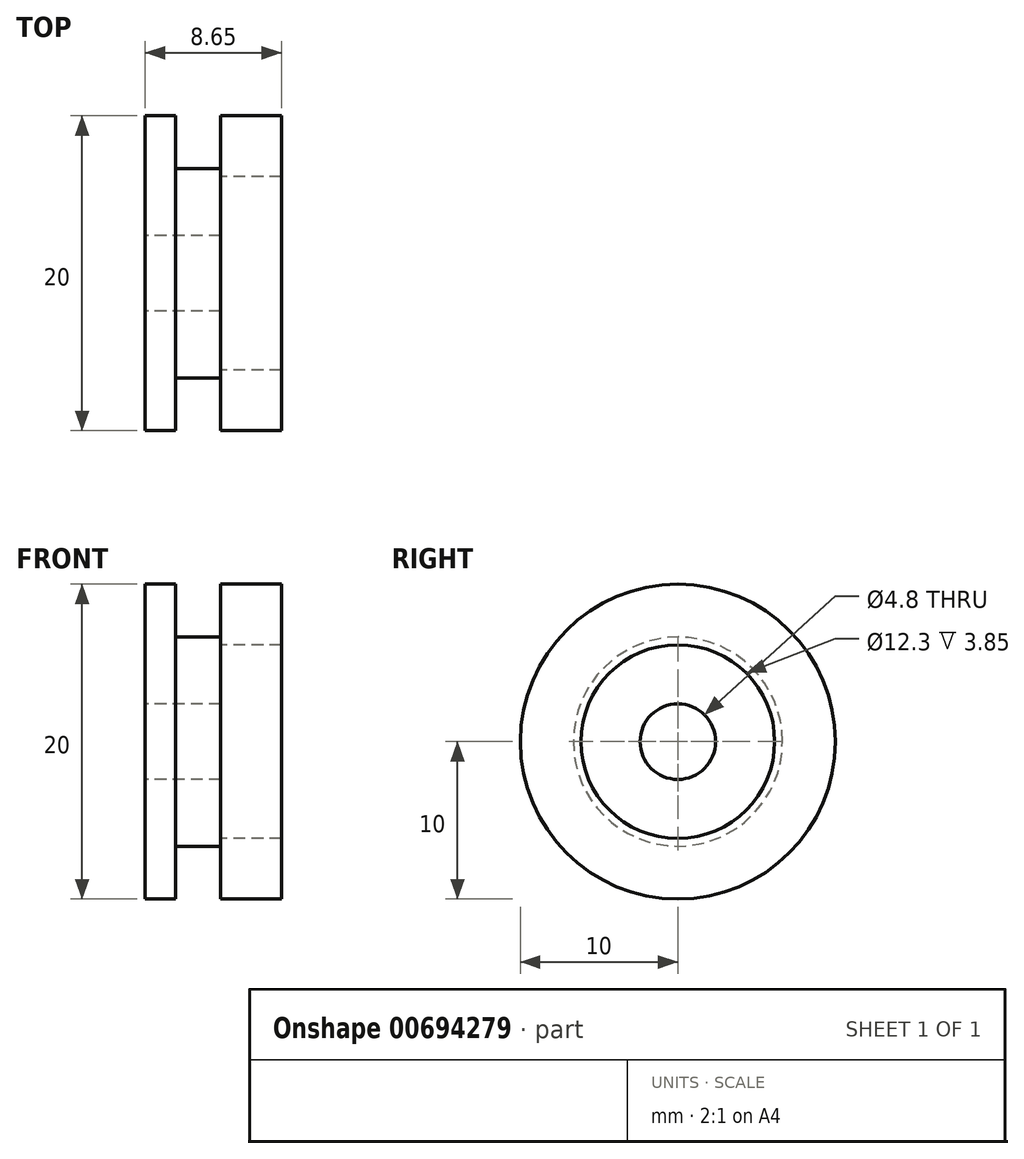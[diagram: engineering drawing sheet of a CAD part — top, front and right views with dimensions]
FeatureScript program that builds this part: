
annotation { "Feature Type Name" : "Feature", "Feature Type Description" : "" }
export const myFeature = defineFeature(function(context is Context, id is Id, definition is map)
    precondition{}
    {
        {
            var Q0;
            Q0=qCreatedBy(makeId("Front.planeOp"),FACE);
            var sketch = newSketch(context, id + "F0", { "sketchPlane" : qUnion([Q0])});
            skLineSegment(sketch, "E0", {"start": v(-5, 0) * mm, "end": v(-5, 10) * mm});
            skLineSegment(sketch, "E1", {"start": v(-5, 10) * mm, "end": v(-3.08, 10) * mm});
            skLineSegment(sketch, "E2", {"start": v(-3.08, 10) * mm, "end": v(-3.08, 6.64) * mm});
            skLineSegment(sketch, "E3", {"start": v(-3.08, 6.64) * mm, "end": v(-0.2, 6.64) * mm});
            skLineSegment(sketch, "E4", {"start": v(-0.2, 6.64) * mm, "end": v(-0.2, 10) * mm});
            skLineSegment(sketch, "E5", {"start": v(-0.2, 10) * mm, "end": v(3.65, 10) * mm});
            skPoint(sketch, "E6.end.orphan", {"position": v(-5, 2.4) * mm});
            skLineSegment(sketch, "E7", {"start": v(3.65, 10) * mm, "end": v(3.65, 6.15) * mm});
            skLineSegment(sketch, "E8", {"start": v(3.65, 6.15) * mm, "end": v(-0.2, 6.15) * mm});
            skLineSegment(sketch, "E9", {"start": v(-0.2, 6.15) * mm, "end": v(-0.2, 2.4) * mm});
            skLineSegment(sketch, "E10", {"start": v(-0.2, 2.4) * mm, "end": v(-5, 2.4) * mm});
            skLineSegment(sketch, "E11", {"start": v(-5, 0) * mm, "end": v(34.3, 0) * mm, "construction": true});
            skSolve(sketch);
        }
        {
            var Q0;
            Q0=qSketchRegion(id+"F0",true);
            var Q1;
            Q1=sQuery(id+"F0.wireOp",EDGE,"E11");
            revolve(context, id + "F1", {"entities" : qUnion([Q0]), "axis" : qUnion([Q1]), "revolveType" : RevolveType.FULL});
        }
    });
